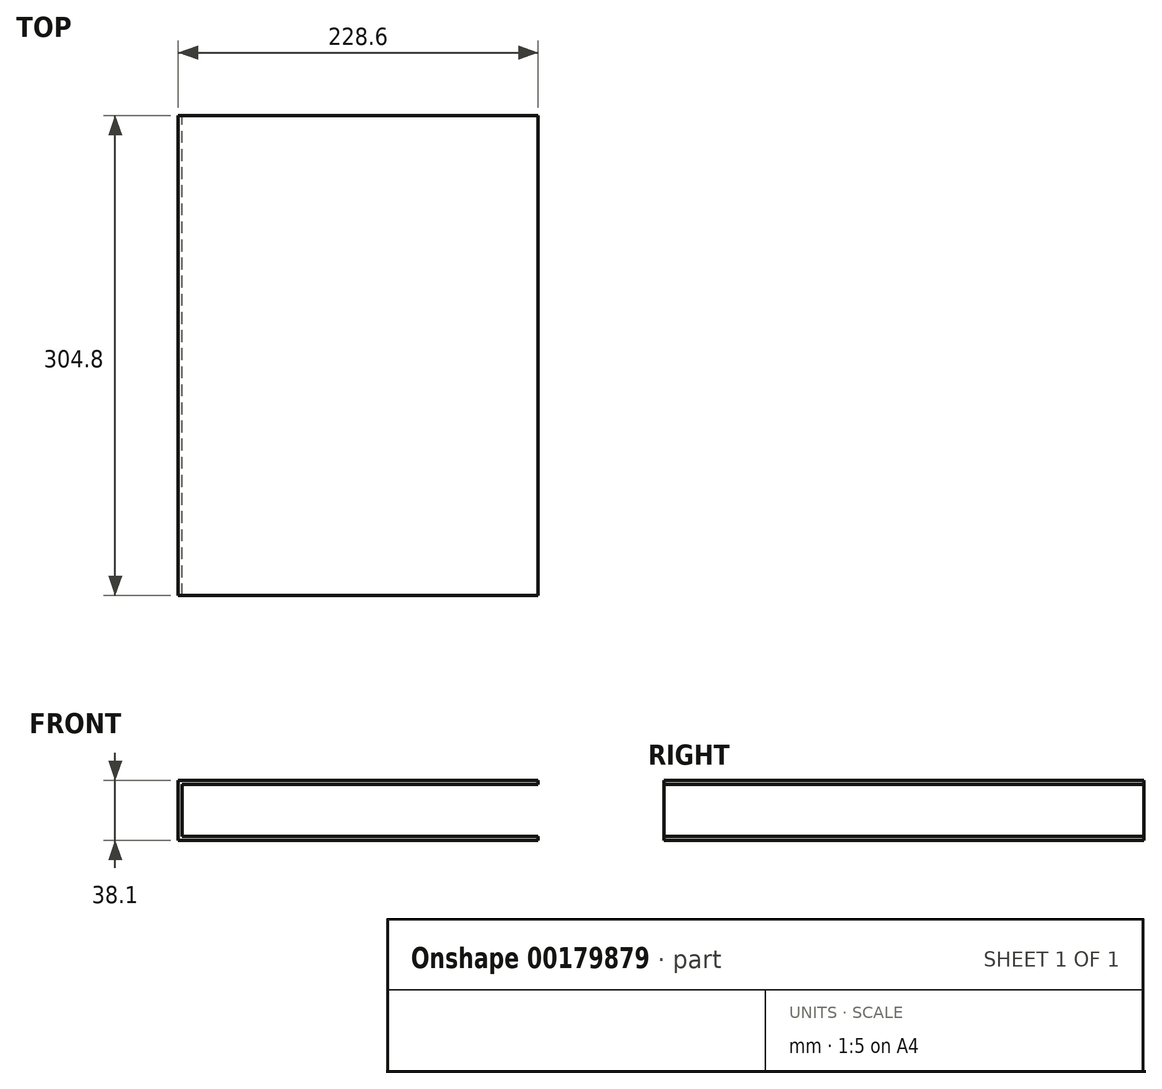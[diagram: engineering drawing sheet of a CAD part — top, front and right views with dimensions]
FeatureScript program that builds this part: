
annotation { "Feature Type Name" : "Feature", "Feature Type Description" : "" }
export const myFeature = defineFeature(function(context is Context, id is Id, definition is map)
    precondition{}
    {
        {
            var Q0;
            Q0=qCreatedBy(makeId("Front.planeOp"),FACE);
            var sketch = newSketch(context, id + "F0", { "sketchPlane" : qUnion([Q0])});
            skLineSegment(sketch, "E0.bottom", {"start": v(-114.3, 19.05) * mm, "end": v(114.3, 19.05) * mm});
            skLineSegment(sketch, "E0.top", {"start": v(-114.3, -19.05) * mm, "end": v(114.3, -19.05) * mm});
            skLineSegment(sketch, "E0.left", {"start": v(-114.3, 19.05) * mm, "end": v(-114.3, -19.05) * mm});
            skPoint(sketch, "E0.middle", {"position": v(0, 0) * mm});
            skLineSegment(sketch, "E1", {"start": v(114.3, 19.05) * mm, "end": v(114.3, 16.51) * mm});
            skLineSegment(sketch, "E2", {"start": v(114.3, 16.51) * mm, "end": v(-111.76, 16.5) * mm});
            skLineSegment(sketch, "E3", {"start": v(-111.76, 16.5) * mm, "end": v(-111.76, -16.51) * mm});
            skLineSegment(sketch, "E4", {"start": v(-111.76, -16.51) * mm, "end": v(114.3, -16.51) * mm});
            skLineSegment(sketch, "E5", {"start": v(114.3, -16.51) * mm, "end": v(114.3, -19.05) * mm});
            skSolve(sketch);
        }
        {
            var Q0;
            Q0 = qSketchRegion(id + "F0", true);
            extrude(context, id + "F1", {"entities" : qUnion([Q0]), "depth" : 304.8 * mm});
        }
    });
